# Revit family: HD044-2016.02.29-BT-Uveline
name_source: partatom
category: Generic Models
revit_build: Autodesk Revit 2016 (Build: 20150714_1515(x64)
units: mm (PartAtom-declared; Revit-internal decimal feet)

## family parameters
Always vertical = Yes
Can host rebar = No
Cut with Voids When Loaded = No
Part Type = Normal
Room Calculation Point = No
Round Connector Dimension = Use Diameter
Shared = No
Work Plane-Based = No

## types (1)
- Productos HD
    BT_Alto = 6 mts maximo
    BT_Ancho = Avance 400 mm
    BT_Codigo_Origen = HD046
    BT_Color = 100 colores a eleccion
    BT_Descripcion = Panel Uveline
    BT_EETT = Panel Uveline
    BT_Elemento = Paneles y Revestimientos verticales
    BT_Especialidad = Arquitectura
    BT_Fabricante = Hunter Douglas
    BT_Itemizado_Estandar_CDT = D 01 08 04
    BT_Linea = A pedido
    BT_Marca = Hunter Douglas
    BT_MasterFormat® = 07 42 13
    BT_Material = Aluzinc
    BT_Nombre_Comercial = Panel Uveline
    BT_Nombre_Corto = Panel Uveline
    BT_Nombre_Tecnico = Panel Uveline
    BT_Profundidad = Largo Máximo 6 mts
    BT_SKU = 00 00 00
    BT_Uso = Exterior
    BT_Web_del_Producto = http://www.hunterdouglas.cl
    Description = Panel Uveline
    Distancia  entre apoyos = 1200 mm
    ID_Objeto = BT_F_F_250
    ID_Source = BIMTOOL
    Largo Panel (Editar Largo en tipo de panel) = 1400 mm  [stored 4.59318 ft]
    Manufacturer = Hunter Douglas
    Material = Metal
    URL = http://www.hunterdouglas.cl

note: [stored X ft] marks values corroborated as IEEE doubles in the binary element streams (Revit-internal decimal feet)

## geometry (parser evidence)
native form markers: Blend x8, Sweep x10
no freeform markers — native parametric forms only
